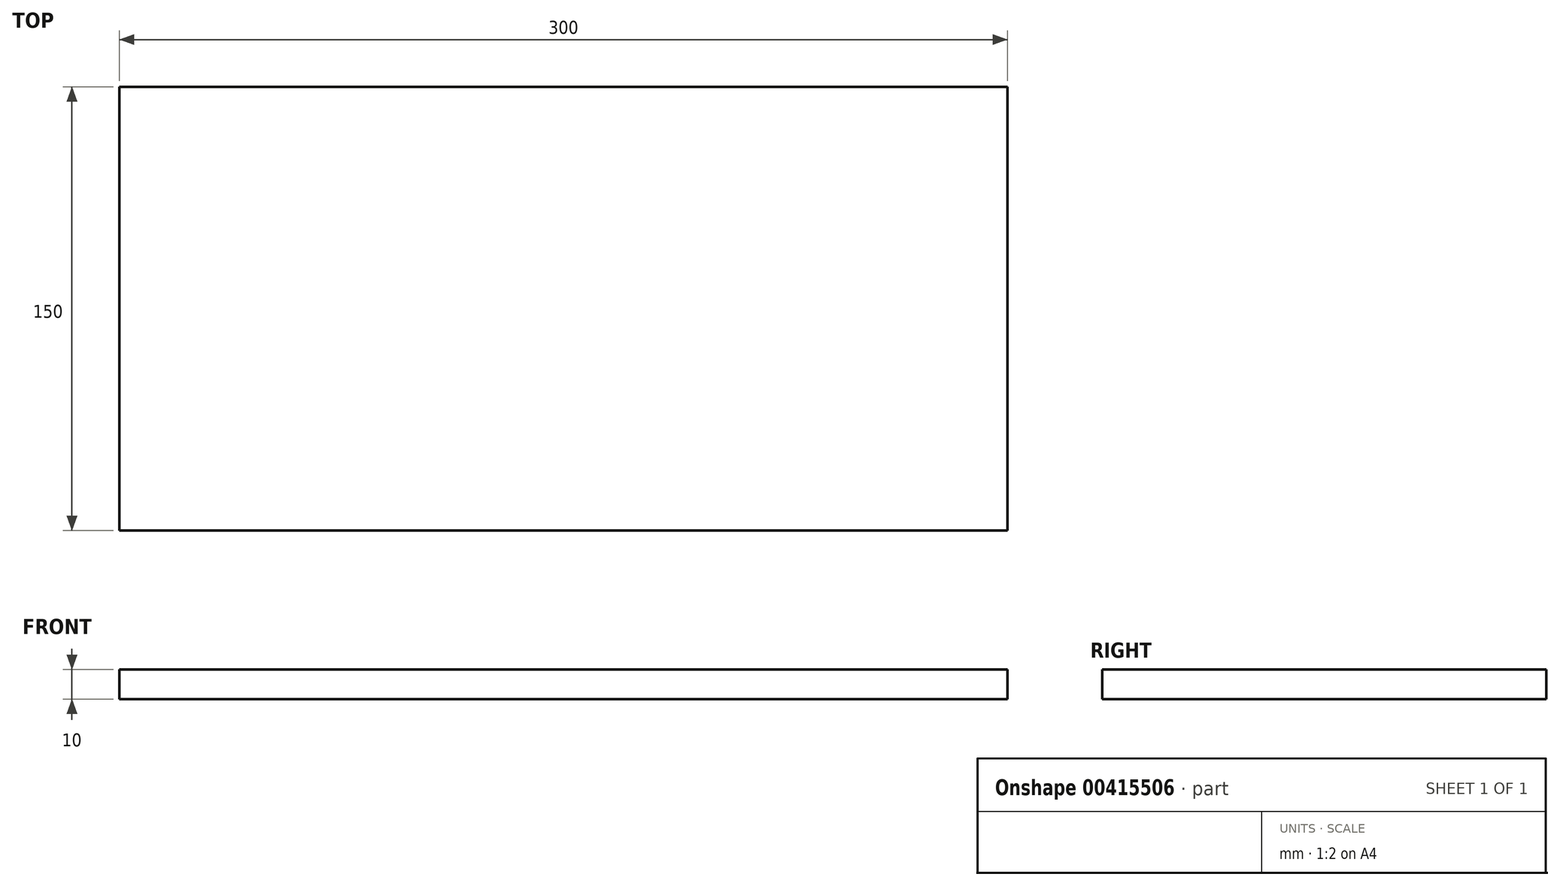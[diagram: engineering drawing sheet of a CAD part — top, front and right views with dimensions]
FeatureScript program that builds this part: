
annotation { "Feature Type Name" : "Feature", "Feature Type Description" : "" }
export const myFeature = defineFeature(function(context is Context, id is Id, definition is map)
    precondition{}
    {
        {
            var Q0;
            Q0=qCreatedBy(makeId("Top.planeOp"),FACE);
            var sketch = newSketch(context, id + "F0", { "sketchPlane" : qUnion([Q0])});
            skLineSegment(sketch, "E0.bottom", {"start": v(0, 0) * mm, "end": v(300, 0) * mm});
            skLineSegment(sketch, "E0.top", {"start": v(0, 150) * mm, "end": v(300, 150) * mm});
            skLineSegment(sketch, "E0.left", {"start": v(0, 0) * mm, "end": v(0, 150) * mm});
            skLineSegment(sketch, "E0.right", {"start": v(300, 0) * mm, "end": v(300, 150) * mm});
            skSolve(sketch);
        }
        {
            var Q0;
            Q0=makeQuery(id+"F0.imprint","IMPRINT",FACE,{"disambiguationData":[TD([[makeQuery(id+"F0.imprint","IMPRINT",EDGE,{"derivedFrom":sQuery(id+"F0.wireOp",EDGE,"E0.bottom")}),1.0]])]});
            extrude(context, id + "F1", {"entities" : qUnion([Q0]), "depth" : 10 * mm});
        }
    });
